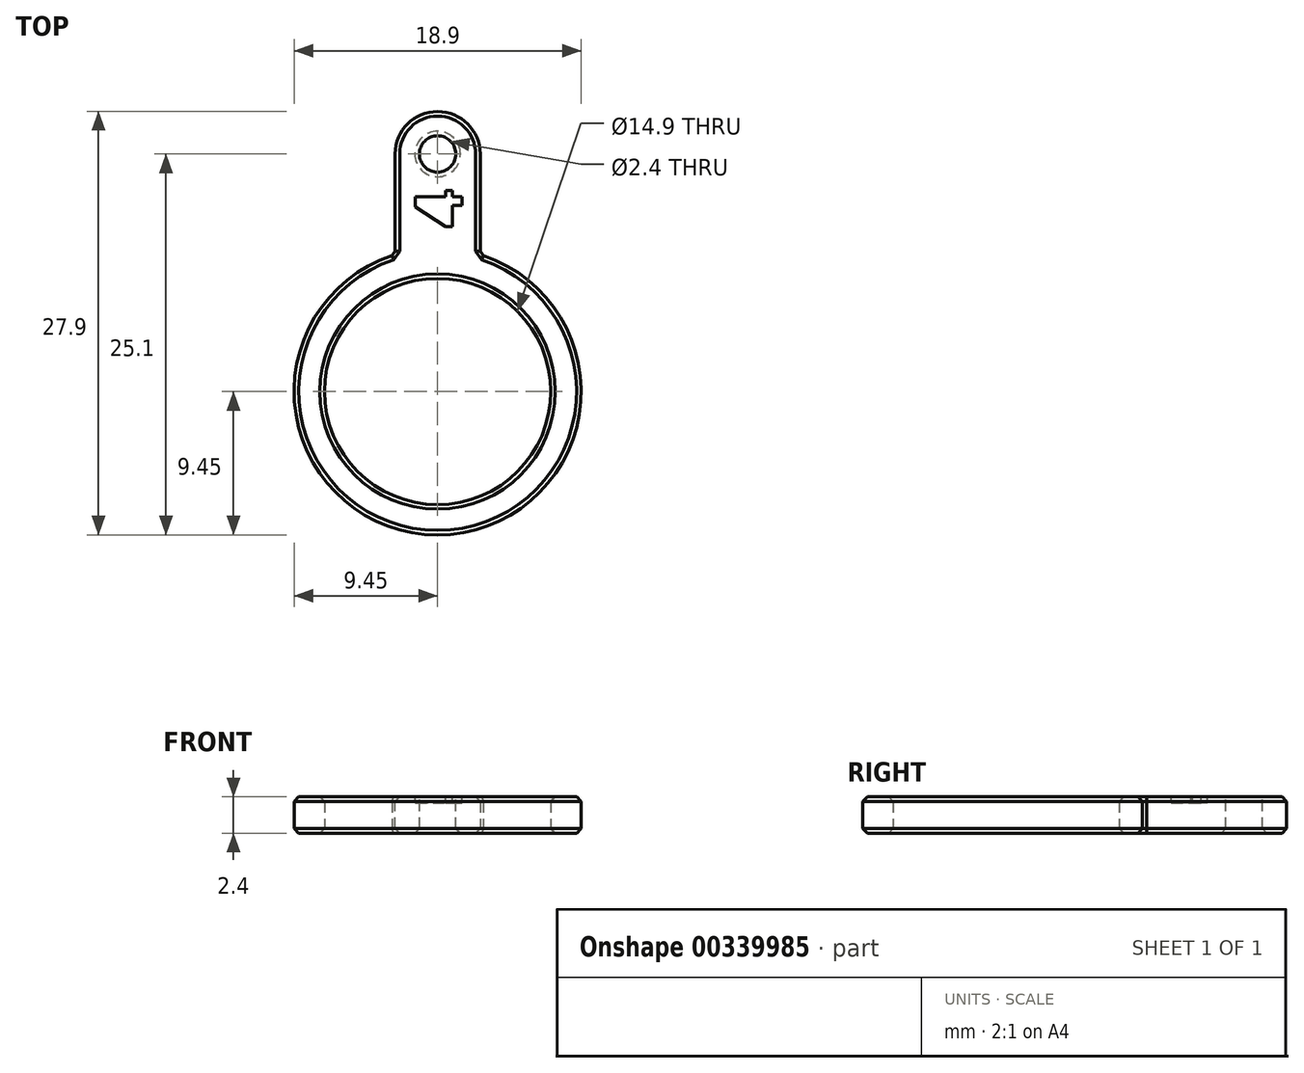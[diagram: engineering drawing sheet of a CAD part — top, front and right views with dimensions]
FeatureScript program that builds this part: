
annotation { "Feature Type Name" : "Feature", "Feature Type Description" : "" }
export const myFeature = defineFeature(function(context is Context, id is Id, definition is map)
    precondition{}
    {
        {
            var Q0;
            Q0=qCreatedBy(makeId("Top.planeOp"),FACE);
            var sketch = newSketch(context, id + "F0", { "sketchPlane" : qUnion([Q0])});
            skCircle(sketch, "E0", {"center": v(0, 0) * mm, "radius": 7.45 * mm});
            skCircle(sketch, "E1", {"center": v(0, 0) * mm, "radius": 9.45 * mm});
            skLineSegment(sketch, "E2.bottom", {"start": v(2.8, 0.45) * mm, "end": v(-2.8, 0.45) * mm});
            skLineSegment(sketch, "E2.top", {"start": v(2.8, 18.45) * mm, "end": v(-2.8, 18.45) * mm});
            skLineSegment(sketch, "E2.left", {"start": v(2.8, 0.45) * mm, "end": v(2.8, 18.45) * mm});
            skLineSegment(sketch, "E2.right", {"start": v(-2.8, 0.45) * mm, "end": v(-2.8, 18.45) * mm});
            skPoint(sketch, "E2.middle", {"position": v(0, 9.45) * mm});
            skSolve(sketch);
        }
        {
            var Q0;
            Q0 = qSketchRegion(id + "F0", true);
            extrude(context, id + "F1", {"entities" : qUnion([Q0]), "depth" : 2.4 * mm});
        }
        {
            var Q0;
            Q0=makeQuery(id+"F1.opExtrude","SWEPT_EDGE",EDGE,{"disambiguationData":[OSD([sQuery(id+"F0.wireOp",EDGE,"E2.top"),sQuery(id+"F0.wireOp",EDGE,"E2.right")])]});
            var Q1;
            Q1=makeQuery(id+"F1.opExtrude","SWEPT_EDGE",EDGE,{"disambiguationData":[OSD([sQuery(id+"F0.wireOp",EDGE,"E2.top"),sQuery(id+"F0.wireOp",EDGE,"E2.left")])]});
            fillet(context, id + "F2", {"entities" : qUnion([Q0, Q1]), "radius" : 2.8 * mm, "tangentPropagation" : true, "allowEdgeOverflow" : false});
        }
        {
            var Q0;
            Q0=makeQuery(id+"F1.opExtrude","CAP_FACE",FACE,{"disambiguationData":[OSD([sQuery(id+"F0.wireOp",EDGE,"E0"),sQuery(id+"F0.wireOp",EDGE,"E1"),sQuery(id+"F0.wireOp",EDGE,"E2.top"),sQuery(id+"F0.wireOp",EDGE,"E2.left"),sQuery(id+"F0.wireOp",EDGE,"E2.right")])],"isStart":false});
            var sketch = newSketch(context, id + "F3", { "sketchPlane" : qUnion([Q0])});
            skCircle(sketch, "E3", {"center": v(0, 15.65) * mm, "radius": 1.2 * mm});
            skSolve(sketch);
        }
        {
            var Q0;
            Q0 = qSketchRegion(id + "F3", true);
            extrude(context, id + "F4", {"entities" : qUnion([Q0]), "operationType" : NewBodyOperationType.REMOVE, "oppositeDirection" : true, "depth" : 25 * mm});
        }
        {
            var Q0;
            Q0=makeQuery(id+"F4.boolean.opBoolean","COPY",EDGE,{"derivedFrom":makeQuery(id+"F4.opExtrude","CAP_EDGE",EDGE,{"disambiguationData":[OSD([sQuery(id+"F3.wireOp",EDGE,"E3")])],"isStart":true})});
            var Q1;
            Q1=makeQuery(id+"F4.boolean.opBoolean","INTERSECT",EDGE,{"derivedFrom":[makeQuery(id+"F1.opExtrude","CAP_FACE",FACE,{"disambiguationData":[OSD([sQuery(id+"F0.wireOp",EDGE,"E0"),sQuery(id+"F0.wireOp",EDGE,"E1"),sQuery(id+"F0.wireOp",EDGE,"E2.top"),sQuery(id+"F0.wireOp",EDGE,"E2.left"),sQuery(id+"F0.wireOp",EDGE,"E2.right")])],"isStart":true}),makeQuery(id+"F4.opExtrude","SWEPT_FACE",FACE,{"disambiguationData":[OSD([sQuery(id+"F3.wireOp",EDGE,"E3")])]})]});
            var Q2;
            {var subQ0=sQuery(id+"F0.wireOp",EDGE,"E2.right");var subQ1=sQuery(id+"F0.wireOp",EDGE,"E2.top");Q2=makeQuery(id+"F2.opFillet","BLEND_EDGE",EDGE,{"blendedFrom":[makeQuery(id+"F1.opExtrude","SWEPT_EDGE",EDGE,{"disambiguationData":[OSD([subQ1,subQ0])]}),makeQuery(id+"F1.opExtrude","CAP_FACE",FACE,{"disambiguationData":[OSD([sQuery(id+"F0.wireOp",EDGE,"E0"),sQuery(id+"F0.wireOp",EDGE,"E1"),subQ1,sQuery(id+"F0.wireOp",EDGE,"E2.left"),subQ0])],"isStart":true})],"blendedInto":[makeQuery(id+"F1.opExtrude","CAP_FACE",FACE,{"disambiguationData":[OSD([sQuery(id+"F0.wireOp",EDGE,"E0"),sQuery(id+"F0.wireOp",EDGE,"E1"),subQ1,sQuery(id+"F0.wireOp",EDGE,"E2.left"),subQ0])],"isStart":true})]});}
            var Q3;
            {var subQ0=sQuery(id+"F0.wireOp",EDGE,"E2.right");var subQ1=sQuery(id+"F0.wireOp",EDGE,"E2.top");Q3=makeQuery(id+"F2.opFillet","BLEND_EDGE",EDGE,{"blendedFrom":[makeQuery(id+"F1.opExtrude","SWEPT_EDGE",EDGE,{"disambiguationData":[OSD([subQ1,subQ0])]}),makeQuery(id+"F1.opExtrude","CAP_FACE",FACE,{"disambiguationData":[OSD([sQuery(id+"F0.wireOp",EDGE,"E0"),sQuery(id+"F0.wireOp",EDGE,"E1"),subQ1,sQuery(id+"F0.wireOp",EDGE,"E2.left"),subQ0])],"isStart":false})],"blendedInto":[makeQuery(id+"F1.opExtrude","CAP_FACE",FACE,{"disambiguationData":[OSD([sQuery(id+"F0.wireOp",EDGE,"E0"),sQuery(id+"F0.wireOp",EDGE,"E1"),subQ1,sQuery(id+"F0.wireOp",EDGE,"E2.left"),subQ0])],"isStart":false})]});}
            var Q4;
            Q4=makeQuery(id+"F1.opExtrude","CAP_EDGE",EDGE,{"disambiguationData":[OSD([sQuery(id+"F0.wireOp",EDGE,"E1")])],"isStart":false});
            var Q5;
            Q5=makeQuery(id+"F1.opExtrude","CAP_EDGE",EDGE,{"disambiguationData":[OSD([sQuery(id+"F0.wireOp",EDGE,"E1")])],"isStart":true});
            var Q6;
            Q6=makeQuery(id+"F1.opExtrude","SWEPT_EDGE",EDGE,{"disambiguationData":[OSD([sQuery(id+"F0.wireOp",EDGE,"E1"),sQuery(id+"F0.wireOp",EDGE,"E2.left")])]});
            var Q7;
            Q7=makeQuery(id+"F1.opExtrude","SWEPT_EDGE",EDGE,{"disambiguationData":[OSD([sQuery(id+"F0.wireOp",EDGE,"E1"),sQuery(id+"F0.wireOp",EDGE,"E2.right")])]});
            var Q8;
            Q8=makeQuery(id+"F1.opExtrude","CAP_EDGE",EDGE,{"disambiguationData":[OSD([sQuery(id+"F0.wireOp",EDGE,"E0")])],"isStart":true});
            var Q9;
            Q9=makeQuery(id+"F1.opExtrude","CAP_EDGE",EDGE,{"disambiguationData":[OSD([sQuery(id+"F0.wireOp",EDGE,"E0")])],"isStart":false});
            chamfer(context, id + "F5", {"entities" : qUnion([Q0, Q1, Q2, Q3, Q4, Q5, Q6, Q7, Q8, Q9]), "width" : 0.3 * mm, "tangentPropagation" : true});
        }
        {
            var Q0;
            Q0=makeQuery(id+"F1.opExtrude","CAP_FACE",FACE,{"disambiguationData":[OSD([sQuery(id+"F0.wireOp",EDGE,"E0"),sQuery(id+"F0.wireOp",EDGE,"E1"),sQuery(id+"F0.wireOp",EDGE,"E2.top"),sQuery(id+"F0.wireOp",EDGE,"E2.left"),sQuery(id+"F0.wireOp",EDGE,"E2.right")])],"isStart":false});
            var sketch = newSketch(context, id + "F6", { "sketchPlane" : qUnion([Q0])});
            skText(sketch, "E4", { "text": "4", "fontName": "Arimo-Bold.ttf"});
            skLineSegment(sketch, "E5", {"start": v(0, 10.8) * mm, "end": v(0, 0) * mm});
            skPoint(sketch, "E5.endSnap0", {"position": v(0, 10.8) * mm});
            const initialGuessF6  = {"E4": [0.0016, 0.0108, 0, 1, 0.0032]};
            skSetInitialGuess(sketch, initialGuessF6);
            skSolve(sketch);
        }
        {
            var Q0;
            Q0 = qSketchRegion(id + "F6", true);
            var Q1;
            Q1=makeQuery(id+"F6.imprint","IMPRINT",FACE,{"disambiguationData":[TD([[makeQuery(id+"F6.imprint","IMPRINT",EDGE,{"derivedFrom":sQuery(id+"F6.wireOp",EDGE,"E4.sketch_text.stroke-11")}),1.0]])]});
            extrude(context, id + "F7", {"entities" : qUnion([Q0, Q1]), "operationType" : NewBodyOperationType.REMOVE, "oppositeDirection" : true, "depth" : 0.4 * mm});
        }
    });
